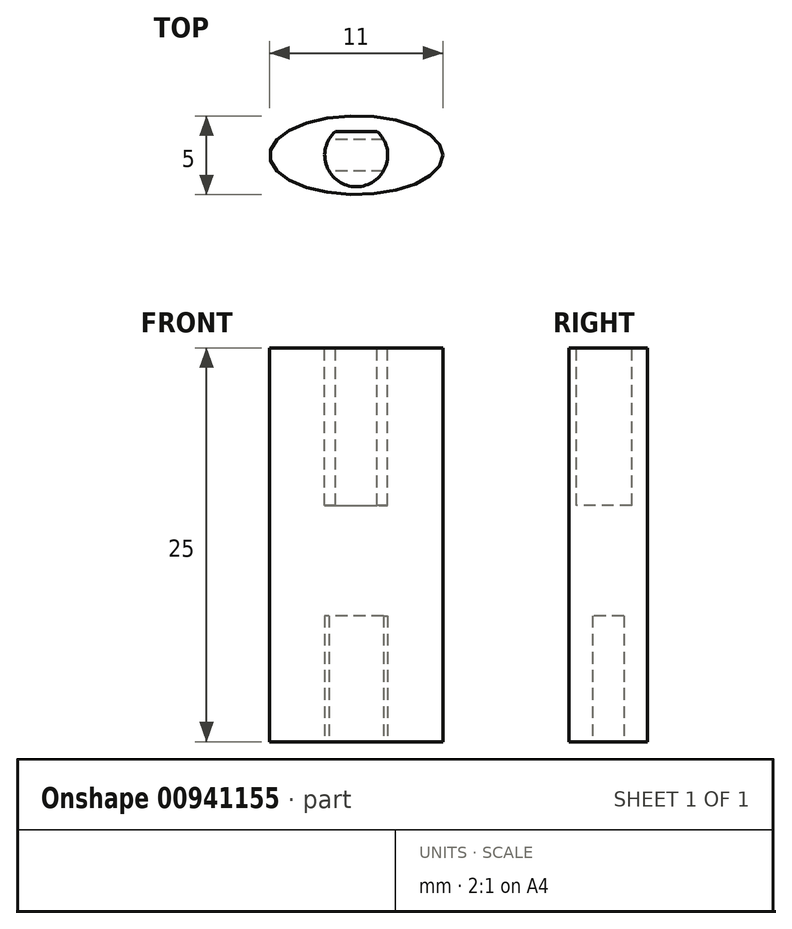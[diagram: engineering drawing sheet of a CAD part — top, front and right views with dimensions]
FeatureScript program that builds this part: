
annotation { "Feature Type Name" : "Feature", "Feature Type Description" : "" }
export const myFeature = defineFeature(function(context is Context, id is Id, definition is map)
    precondition{}
    {
        {
            var Q0;
            Q0=qCreatedBy(makeId("Top.planeOp"),FACE);
            var sketch = newSketch(context, id + "F0", { "sketchPlane" : qUnion([Q0])});
            skEllipse(sketch, "E0", {"center": v(0, 0) * mm, "majorRadius": 5.5 * mm, "minorRadius": 2.5 * mm, "majorAxis": v(1, 0)});
            skSolve(sketch);
        }
        {
            var Q0;
            Q0 = qSketchRegion(id + "F0", true);
            extrude(context, id + "F1", {"entities" : qUnion([Q0]), "depth" : 25 * mm, "offsetDistance" : 25 * mm});
        }
        {
            var Q0;
            Q0=makeQuery(id+"F1.opExtrude","CAP_FACE",FACE,{"disambiguationData":[OSD([sQuery(id+"F0.wireOp",EDGE,"E0")])],"isStart":false});
            var sketch = newSketch(context, id + "F2", { "sketchPlane" : qUnion([Q0])});
            skSolve(sketch);
        }
        {
            var Q0;
            Q0=makeQuery(id+"F2.imprint","IMPRINT",FACE,{"disambiguationData":[TD([[makeQuery(id+"F2.imprint","IMPRINT",EDGE,{"derivedFrom":makeQuery(id+"F1.opExtrude","CAP_EDGE",EDGE,{"disambiguationData":[OSD([sQuery(id+"F0.wireOp",EDGE,"E0")])],"isStart":false})}),1.0]])]});
            var sketch = newSketch(context, id + "F3", { "sketchPlane" : qUnion([Q0])});
            skArc(sketch, "E1", {"start": v(-1.32, 1.5) * mm, "mid": v(0, -2) * mm, "end": v(1.32, 1.5) * mm});
            skLineSegment(sketch, "E2", {"start": v(0, -1.5) * mm, "end": v(0, 1.5) * mm});
            skLineSegment(sketch, "E3", {"start": v(0, 1.5) * mm, "end": v(-1.32, 1.5) * mm});
            skLineSegment(sketch, "E4", {"start": v(-1.32, 1.5) * mm, "end": v(1.32, 1.5) * mm});
            skLineSegment(sketch, "E5", {"start": v(0, 0) * mm, "end": v(0, -1.5) * mm});
            skLineSegment(sketch, "E6", {"start": v(-1.32, -1.5) * mm, "end": v(1.32, -1.5) * mm});
            skPoint(sketch, "E7.orphan", {"position": v(-2.63, -1.5) * mm});
            skPoint(sketch, "E8.orphan", {"position": v(0, -2) * mm});
            skSolve(sketch);
        }
        {
            var Q0;
            {var subQ0=sQuery(id+"F3.wireOp",EDGE,"E4");Q0=makeQuery(id+"F3.imprint","IMPRINT",FACE,{"disambiguationData":[TD([[makeQuery(id+"F3.imprint","IMPRINT",EDGE,{"derivedFrom":subQ0}),-1.0]])]});}
            var Q1;
            {var subQ0=sQuery(id+"F3.wireOp",EDGE,"E3");Q1=makeQuery(id+"F3.imprint","IMPRINT",FACE,{"disambiguationData":[TD([[makeQuery(id+"F3.imprint","IMPRINT",EDGE,{"derivedFrom":subQ0}),1.0]])]});}
            var Q2;
            {var subQ0=sQuery(id+"F3.wireOp",EDGE,"E6");var subQ1=sQuery(id+"F3.wireOp",EDGE,"E1");var subQ2=makeQuery(id+"F3.imprint","INTERSECT",VERTEX,{"disambiguationData":[OD(0.0)],"derivedFrom":[subQ1,subQ0]});Q2=makeQuery(id+"F3.imprint","IMPRINT",FACE,{"disambiguationData":[TD([[makeQuery(id+"F3.imprint","IMPRINT",EDGE,{"disambiguationData":[TD([[subQ2,-1.0]])],"derivedFrom":subQ1}),1.0]])]});}
            extrude(context, id + "F4", {"entities" : qUnion([Q0, Q1, Q2]), "operationType" : NewBodyOperationType.REMOVE, "oppositeDirection" : true, "depth" : 10 * mm, "offsetDistance" : 25 * mm});
        }
        {
            var Q0;
            Q0=makeQuery(id+"F1.opExtrude","CAP_FACE",FACE,{"disambiguationData":[OSD([sQuery(id+"F0.wireOp",EDGE,"E0")])],"isStart":true});
            var sketch = newSketch(context, id + "F5", { "sketchPlane" : qUnion([Q0])});
            skArc(sketch, "E9", {"start": v(-1.73, 1) * mm, "mid": v(-2, 0) * mm, "end": v(-1.73, -1) * mm});
            skLineSegment(sketch, "E10", {"start": v(0, 0) * mm, "end": v(0, -1) * mm});
            skLineSegment(sketch, "E11", {"start": v(0, 0) * mm, "end": v(0, 1) * mm});
            skLineSegment(sketch, "E12", {"start": v(1.73, 1) * mm, "end": v(-1.73, 1) * mm});
            skLineSegment(sketch, "E13", {"start": v(1.73, -1) * mm, "end": v(-1.73, -1) * mm});
            skPoint(sketch, "E14.orphan", {"position": v(2.4, -1) * mm});
            skPoint(sketch, "E15.orphan", {"position": v(2.77, 1) * mm});
            skArc(sketch, "E16.trimOffspring", {"start": v(1.73, -1) * mm, "mid": v(2, 0) * mm, "end": v(1.73, 1) * mm});
            skSolve(sketch);
        }
        {
            var Q0;
            Q0 = qSketchRegion(id + "F5", true);
            extrude(context, id + "F6", {"entities" : qUnion([Q0]), "operationType" : NewBodyOperationType.REMOVE, "oppositeDirection" : true, "depth" : 8 * mm, "offsetDistance" : 25 * mm});
        }
    });
